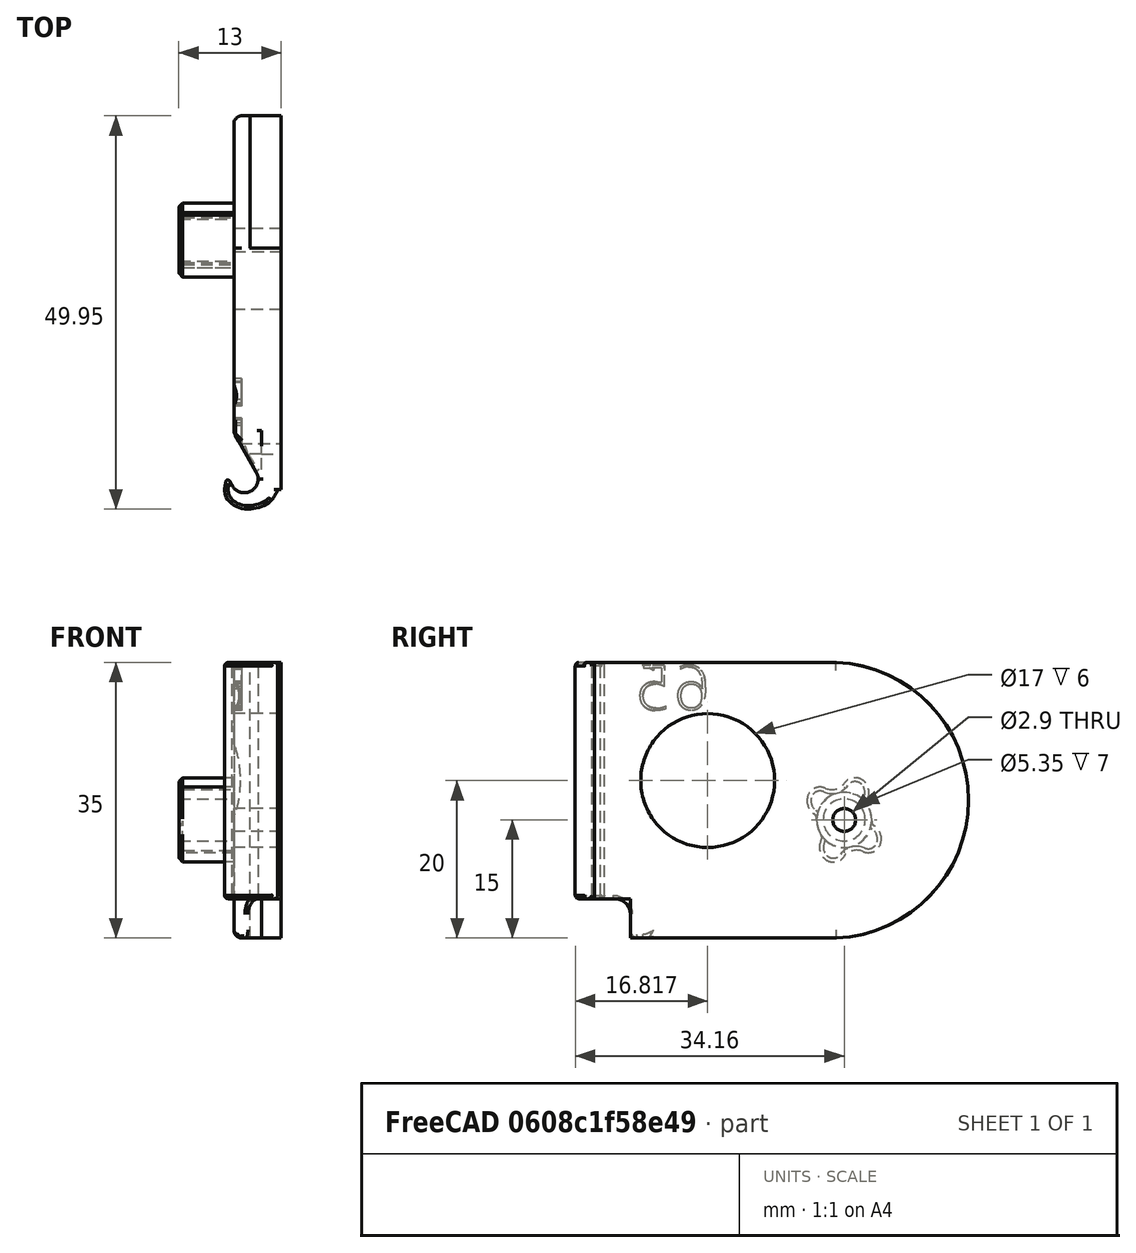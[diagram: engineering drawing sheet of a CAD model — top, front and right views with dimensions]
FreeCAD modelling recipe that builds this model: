
FCSTD DOCUMENT  (FreeCAD 0.18R)
Label: hinge-left-165deg-flat
License: All rights reserved
LicenseURL: http://en.wikipedia.org/wiki/All_rights_reserved
objects: App::FeaturePython×4, Part::FeaturePython×2, Part::Part2DObjectPython×1, Part::Extrusion×1, Part::Cut×1
note: 5 computed .brp shape members not serialized (recipe doc carries the construction recipe); baked Part::Feature solids carry a one-line shape summary decoded from their .brp

FEATURE [Part::FeaturePython] pillar_base_001  label="pillar-base_001"  # a2plus imported part (geometry in sourceFile) (typed FeaturePython)
  Placement = pos=(0.000608724,-2.19081,4.98403) rot=(-1,0,0;0.174707rad)
  a2p_Version = V0.1
  fixedPosition = false
  objectType = a2pPart
  sourceFile = ./parts/pillar-base.fcstd
  subassemblyImport = false
  timeLastImport = 1.60452e+09
  updateColors = true
FEATURE [Part::Part2DObjectPython] ShapeString  # Draft 2D object (typed FeaturePython)
  FontFile = <path>
  Placement = pos=(1.61,10.5,29) rot=(0.57735,-0.57735,-0.57735;2.0944rad)
  Size = 6
  String = 65
  Tracking = 0
FEATURE [Part::Extrusion] Extrude
  Base = -> ShapeString
  Dir = (-1,0,0)
  DirMode = 2
  FaceMakerClass = Part::FaceMakerBullseye
  LengthFwd = 2
  LengthRev = 0
  Solid = false
  Symmetric = false
FEATURE [Part::FeaturePython] bracket_left_flat_001  label="bracket-left-flat_001"  # a2plus imported part (geometry in sourceFile) (typed FeaturePython)
  a2p_Version = V0.1
  fixedPosition = true
  objectType = a2pPart
  sourceFile = ./parts/bracket-left-flat.fcstd
  subassemblyImport = false
  timeLastImport = 1.60454e+09
  updateColors = true
FEATURE [App::FeaturePython] axisCoincident_001  label="axisCoincident_001__bracket-left-flat_001"  # a2plus constraint (typed FeaturePython)
  Object1 = pillar_base_001
  Object2 = bracket_left_flat_001
  ParentTreeObject = -> pillar_base_001
  SubElement1 = Face17
  SubElement2 = Face48
  Suppressed = false
  Type = axial
  directionConstraint = 1
  lockRotation = false
FEATURE [App::FeaturePython] axisCoincident_001_mirror  label="axisCoincident_001__pillar-base_001"  # a2plus constraint (typed FeaturePython)
  Object1 = pillar_base_001
  Object2 = bracket_left_flat_001
  ParentTreeObject = -> bracket_left_flat_001
  SubElement1 = Face17
  SubElement2 = Face48
  Suppressed = false
  Type = axial
  directionConstraint = 1
  lockRotation = false
FEATURE [App::FeaturePython] planeCoincident_001  label="planeCoincident_001__bracket-left-flat_001"  # a2plus constraint (typed FeaturePython)
  Object1 = pillar_base_001
  Object2 = bracket_left_flat_001
  ParentTreeObject = -> pillar_base_001
  SubElement1 = Face1
  SubElement2 = Face72
  Suppressed = false
  Type = plane
  directionConstraint = 0
  offset = 0
FEATURE [App::FeaturePython] planeCoincident_001_mirror  label="planeCoincident_001__pillar-base_001"  # a2plus constraint (typed FeaturePython)
  Object1 = pillar_base_001
  Object2 = bracket_left_flat_001
  ParentTreeObject = -> bracket_left_flat_001
  SubElement1 = Face1
  SubElement2 = Face72
  Suppressed = false
  Type = plane
  directionConstraint = 0
  offset = 0
FEATURE [Part::Cut] Cut
  Base = -> bracket_left_flat_001
  Tool = -> Extrude
note: 1 file-system path scrubbed to <path> (originals preserved in the JSON sidecar)
